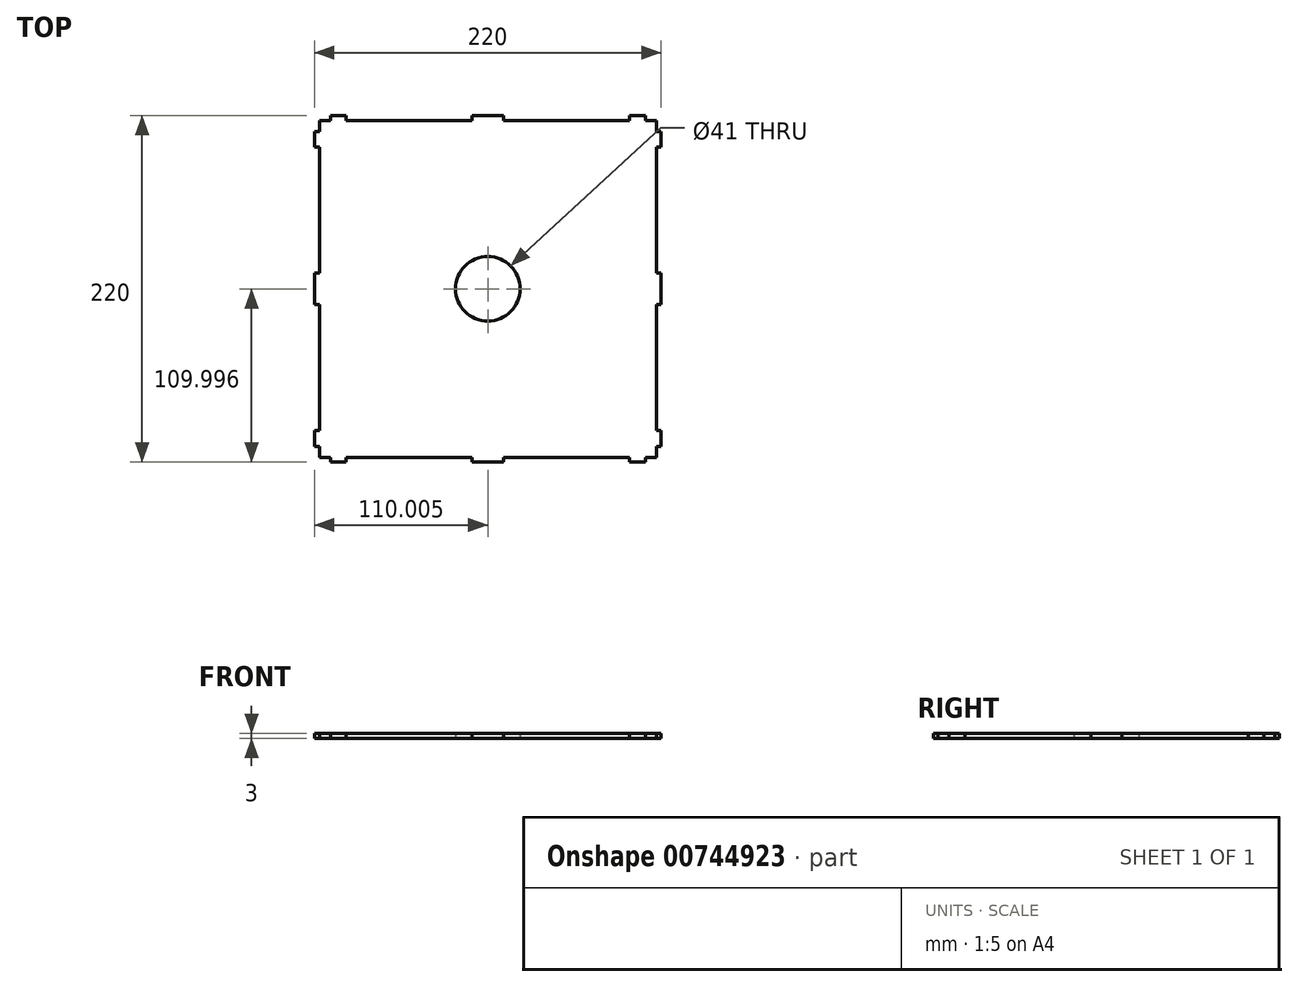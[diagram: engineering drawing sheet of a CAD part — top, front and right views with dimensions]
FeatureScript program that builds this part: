
annotation { "Feature Type Name" : "Feature", "Feature Type Description" : "" }
export const myFeature = defineFeature(function(context is Context, id is Id, definition is map)
    precondition{}
    {
        {
            var Q0;
            Q0=qCreatedBy(makeId("Top.planeOp"),FACE);
            var sketch = newSketch(context, id + "F0", { "sketchPlane" : qUnion([Q0])});
            skLineSegment(sketch, "E0.bottom", {"start": v(-107, 107.1) * mm, "end": v(107, 107.1) * mm, "construction": true});
            skLineSegment(sketch, "E0.top", {"start": v(-107, -106.9) * mm, "end": v(107, -106.9) * mm, "construction": true});
            skLineSegment(sketch, "E0.left", {"start": v(-107, 107.1) * mm, "end": v(-107, -106.9) * mm, "construction": true});
            skLineSegment(sketch, "E0.right", {"start": v(107, 107.1) * mm, "end": v(107, -106.9) * mm, "construction": true});
            skLineSegment(sketch, "E1", {"start": v(-107, 107.1) * mm, "end": v(107, 107.1) * mm});
            skLineSegment(sketch, "E2", {"start": v(107, -106.9) * mm, "end": v(-107, -106.9) * mm});
            skLineSegment(sketch, "E3", {"start": v(-107, -106.9) * mm, "end": v(-107, 107.1) * mm});
            skLineSegment(sketch, "E4", {"start": v(107, 107.1) * mm, "end": v(107, -106.9) * mm});
            skLineSegment(sketch, "E5", {"start": v(-177.77, 0.1) * mm, "end": v(243.32, 0.1) * mm, "construction": true});
            skLineSegment(sketch, "E6", {"start": v(0, 136.41) * mm, "end": v(0, -158.54) * mm, "construction": true});
            skCircle(sketch, "E7", {"center": v(0, 0.1) * mm, "radius": 20.5 * mm});
            skLineSegment(sketch, "E8.bottom", {"start": v(-107, 107.1) * mm, "end": v(-85.14, 107.1) * mm});
            skLineSegment(sketch, "E8.top", {"start": v(-107, 116.06) * mm, "end": v(-85.14, 116.06) * mm});
            skLineSegment(sketch, "E8.left", {"start": v(-107, 107.1) * mm, "end": v(-107, 116.06) * mm});
            skLineSegment(sketch, "E8.right", {"start": v(-85.14, 107.1) * mm, "end": v(-85.14, 116.06) * mm});
            skSolve(sketch);
        }
        {
            var Q0;
            Q0=makeQuery(id+"F0.imprint","IMPRINT",FACE,{"disambiguationData":[TD([[makeQuery(id+"F0.imprint","IMPRINT",EDGE,{"derivedFrom":sQuery(id+"F0.wireOp",EDGE,"E1")}),-1.0]])]});
            extrude(context, id + "F1", {"entities" : qUnion([Q0]), "depth" : 3 * mm, "offsetDistance" : 25 * mm});
        }
        {
            var Q0;
            Q0=makeQuery(id+"F1.opExtrude","CAP_FACE",FACE,{"disambiguationData":[OSD([sQuery(id+"F0.wireOp",EDGE,"E1"),sQuery(id+"F0.wireOp",EDGE,"E2"),sQuery(id+"F0.wireOp",EDGE,"E3"),sQuery(id+"F0.wireOp",EDGE,"E4"),sQuery(id+"F0.wireOp",EDGE,"E7"),sQuery(id+"F0.wireOp",EDGE,"E8.bottom")])],"isStart":false});
            var sketch = newSketch(context, id + "F2", { "sketchPlane" : qUnion([Q0])});
            skLineSegment(sketch, "E9", {"start": v(-195.96, 0.1) * mm, "end": v(228.94, 0.1) * mm, "construction": true});
            skLineSegment(sketch, "E10", {"start": v(0, 149.25) * mm, "end": v(0, -160.12) * mm, "construction": true});
            skLineSegment(sketch, "E11", {"start": v(-90, 131.47) * mm, "end": v(-90, -122.26) * mm, "construction": true});
            skLineSegment(sketch, "E12", {"start": v(-134.06, -89.9) * mm, "end": v(168.47, -89.9) * mm, "construction": true});
            skLineSegment(sketch, "E13.bottom", {"start": v(0, 107.1) * mm, "end": v(-10, 107.1) * mm});
            skLineSegment(sketch, "E13.top", {"start": v(0, 110.1) * mm, "end": v(-10, 110.1) * mm});
            skLineSegment(sketch, "E13.left", {"start": v(0, 107.1) * mm, "end": v(0, 110.1) * mm});
            skLineSegment(sketch, "E13.right", {"start": v(-10, 107.1) * mm, "end": v(-10, 110.1) * mm});
            skLineSegment(sketch, "E14.bottom", {"start": v(-90, 107.1) * mm, "end": v(-100, 107.1) * mm});
            skLineSegment(sketch, "E14.top", {"start": v(-90, 110.1) * mm, "end": v(-100, 110.1) * mm});
            skLineSegment(sketch, "E14.left", {"start": v(-90, 107.1) * mm, "end": v(-90, 110.1) * mm});
            skLineSegment(sketch, "E14.right", {"start": v(-100, 107.1) * mm, "end": v(-100, 110.1) * mm});
            skLineSegment(sketch, "E15.MirrorCS", {"start": v(100, 107.1) * mm, "end": v(100, 110.1) * mm});
            skLineSegment(sketch, "E16.MirrorCS", {"start": v(90, 107.1) * mm, "end": v(90, 110.1) * mm});
            skLineSegment(sketch, "E17.MirrorCS", {"start": v(90, 110.1) * mm, "end": v(100, 110.1) * mm});
            skLineSegment(sketch, "E18.MirrorCS", {"start": v(90, 107.1) * mm, "end": v(100, 107.1) * mm});
            skLineSegment(sketch, "E19.MirrorCS", {"start": v(10, 107.1) * mm, "end": v(10, 110.1) * mm});
            skLineSegment(sketch, "E20.MirrorCS", {"start": v(0, 107.1) * mm, "end": v(10, 107.1) * mm});
            skLineSegment(sketch, "E21.MirrorCS", {"start": v(0, 110.1) * mm, "end": v(10, 110.1) * mm});
            skLineSegment(sketch, "E22.MirrorCS", {"start": v(0, -106.9) * mm, "end": v(0, -109.9) * mm});
            skLineSegment(sketch, "E23.MirrorCS", {"start": v(-10, -106.9) * mm, "end": v(-10, -109.9) * mm});
            skLineSegment(sketch, "E24.MirrorCS", {"start": v(-90, -106.9) * mm, "end": v(-90, -109.9) * mm});
            skLineSegment(sketch, "E25.MirrorCS", {"start": v(-100, -106.9) * mm, "end": v(-100, -109.9) * mm});
            skLineSegment(sketch, "E26.MirrorCS", {"start": v(90, -106.9) * mm, "end": v(90, -109.9) * mm});
            skLineSegment(sketch, "E27.MirrorCS", {"start": v(100, -106.9) * mm, "end": v(100, -109.9) * mm});
            skLineSegment(sketch, "E28.MirrorCS", {"start": v(10, -106.9) * mm, "end": v(10, -109.9) * mm});
            skLineSegment(sketch, "E29.MirrorCS", {"start": v(90, -109.9) * mm, "end": v(100, -109.9) * mm});
            skLineSegment(sketch, "E30.MirrorCS", {"start": v(90, -106.9) * mm, "end": v(100, -106.9) * mm});
            skLineSegment(sketch, "E31.MirrorCS", {"start": v(0, -106.9) * mm, "end": v(-10, -106.9) * mm});
            skLineSegment(sketch, "E32.MirrorCS", {"start": v(0, -109.9) * mm, "end": v(-10, -109.9) * mm});
            skLineSegment(sketch, "E33.MirrorCS", {"start": v(-90, -106.9) * mm, "end": v(-100, -106.9) * mm});
            skLineSegment(sketch, "E34.MirrorCS", {"start": v(-90, -109.9) * mm, "end": v(-100, -109.9) * mm});
            skLineSegment(sketch, "E35.MirrorCS", {"start": v(0, -106.9) * mm, "end": v(10, -106.9) * mm});
            skLineSegment(sketch, "E36.MirrorCS", {"start": v(0, -109.9) * mm, "end": v(10, -109.9) * mm});
            skLineSegment(sketch, "E37.bottom", {"start": v(-107, 0.1) * mm, "end": v(-110, 0.1) * mm});
            skLineSegment(sketch, "E37.top", {"start": v(-107, -9.9) * mm, "end": v(-110, -9.9) * mm});
            skLineSegment(sketch, "E37.left", {"start": v(-107, 0.1) * mm, "end": v(-107, -9.9) * mm});
            skLineSegment(sketch, "E37.right", {"start": v(-110, 0.1) * mm, "end": v(-110, -9.9) * mm});
            skLineSegment(sketch, "E38.bottom", {"start": v(-107, -89.9) * mm, "end": v(-110, -89.9) * mm});
            skLineSegment(sketch, "E38.top", {"start": v(-107, -99.9) * mm, "end": v(-110, -99.9) * mm});
            skLineSegment(sketch, "E38.left", {"start": v(-107, -89.9) * mm, "end": v(-107, -99.9) * mm});
            skLineSegment(sketch, "E38.right", {"start": v(-110, -89.9) * mm, "end": v(-110, -99.9) * mm});
            skLineSegment(sketch, "E39.MirrorCS", {"start": v(-107, 100.1) * mm, "end": v(-110, 100.1) * mm});
            skLineSegment(sketch, "E40.MirrorCS", {"start": v(-107, 90.1) * mm, "end": v(-110, 90.1) * mm});
            skLineSegment(sketch, "E41.MirrorCS", {"start": v(-107, 10.1) * mm, "end": v(-110, 10.1) * mm});
            skLineSegment(sketch, "E42.MirrorCS", {"start": v(-110, 90.1) * mm, "end": v(-110, 100.1) * mm});
            skLineSegment(sketch, "E43.MirrorCS", {"start": v(-110, 0.1) * mm, "end": v(-110, 10.1) * mm});
            skLineSegment(sketch, "E44.MirrorCS", {"start": v(-107, 90.1) * mm, "end": v(-107, 100.1) * mm});
            skLineSegment(sketch, "E45.MirrorCS", {"start": v(-107, 0.1) * mm, "end": v(-107, 10.1) * mm});
            skLineSegment(sketch, "E46.MirrorCS", {"start": v(107, 0.1) * mm, "end": v(110, 0.1) * mm});
            skLineSegment(sketch, "E47.MirrorCS", {"start": v(107, -9.9) * mm, "end": v(110, -9.9) * mm});
            skLineSegment(sketch, "E48.MirrorCS", {"start": v(107, 10.1) * mm, "end": v(110, 10.1) * mm});
            skLineSegment(sketch, "E49.MirrorCS", {"start": v(107, 90.1) * mm, "end": v(110, 90.1) * mm});
            skLineSegment(sketch, "E50.MirrorCS", {"start": v(107, -89.9) * mm, "end": v(110, -89.9) * mm});
            skLineSegment(sketch, "E51.MirrorCS", {"start": v(107, -99.9) * mm, "end": v(110, -99.9) * mm});
            skLineSegment(sketch, "E52.MirrorCS", {"start": v(107, 100.1) * mm, "end": v(110, 100.1) * mm});
            skLineSegment(sketch, "E53.MirrorCS", {"start": v(107, -89.9) * mm, "end": v(107, -99.9) * mm});
            skLineSegment(sketch, "E54.MirrorCS", {"start": v(110, -89.9) * mm, "end": v(110, -99.9) * mm});
            skLineSegment(sketch, "E55.MirrorCS", {"start": v(107, 0.1) * mm, "end": v(107, 10.1) * mm});
            skLineSegment(sketch, "E56.MirrorCS", {"start": v(107, 90.1) * mm, "end": v(107, 100.1) * mm});
            skLineSegment(sketch, "E57.MirrorCS", {"start": v(110, 90.1) * mm, "end": v(110, 100.1) * mm});
            skLineSegment(sketch, "E58.MirrorCS", {"start": v(110, 0.1) * mm, "end": v(110, -9.9) * mm});
            skLineSegment(sketch, "E59.MirrorCS", {"start": v(110, 0.1) * mm, "end": v(110, 10.1) * mm});
            skLineSegment(sketch, "E60.MirrorCS", {"start": v(107, 0.1) * mm, "end": v(107, -9.9) * mm});
            skSolve(sketch);
        }
        {
            var Q0;
            Q0 = qSketchRegion(id + "F2", true);
            extrude(context, id + "F3", {"entities" : qUnion([Q0]), "operationType" : NewBodyOperationType.ADD, "oppositeDirection" : true, "depth" : 3 * mm, "offsetDistance" : 25 * mm});
        }
    });
